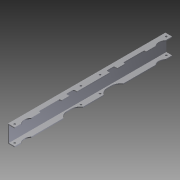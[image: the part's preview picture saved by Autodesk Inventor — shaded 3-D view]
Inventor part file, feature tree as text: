
AUTODESK INVENTOR PART (.ipt)
format: ipt  version: 2012 (Build 160160000, 160)  size: 177,664 bytes
history: native  units: in
note: dims shown in document units (in); Inventor stores cm internally (conversion verified against a paired STEP export)
features: extrude x3, sketch x3, fillet x1
ambient origin geometry x8: Origin, YZ Plane, XZ Plane, XY Plane, X Axis, Y Axis, Z Axis, Center Point
bodies: Solid1 (feature_tree)
feature tree (7):
  extrude  "Extrusion1"  Depth=20.5in TaperAngle=0.0deg
  extrude  "Extrusion2"  Depth=1.5in
  extrude  "Extrusion3"  Depth=0.125in TaperAngle=0.0deg
  fillet  "Fillet1"  Radius=10.25in
  sketch  "Sketch1"  dims[d0=0.125in d1=0.125in d2=0.125in d3=2.25in d4=0.875in d5=20.5in d6=0.0in]
  sketch  "Sketch2"  dims[d7=3.375in d8=2.75in d9=0.25in d10=7.125in d11=1.0in d12=1.0in d13=1.5in d14=0.375in d15=0.25in d16=9.0in d17=1.5in]
  sketch  "Sketch3"  dims[d18=0.45in d19=0.125in d20=0.0in d21=10.25in d22=1.25in d23=0.5in d24=7.375in d25=0.3125in d26=1.5in d27=1.5in d28=1.0in d29=10.25in d30=0.125in d31=0.0in d32=0.125in]
